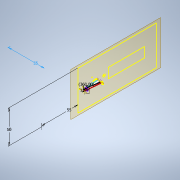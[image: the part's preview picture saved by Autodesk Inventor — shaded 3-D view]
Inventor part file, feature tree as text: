
AUTODESK INVENTOR PART (.ipt)
format: ipt  version: 2021 (Build 250183000, 183)  size: 411,136 bytes
history: native  units: mm
features: other x14, sketch x12, sweep x4, reference x2
ambient origin geometry x8: Origin, YZ Plane, XZ Plane, XY Plane, X Axis, Y Axis, Z Axis, Center Point
bodies: Body1 (feature_tree)
feature tree (32):
  sketch  "Szkic1"
  other  "Płaszczyzna konstrukcyjna1"
  sketch  "Szkic2"
  other  "Płaszczyzna konstrukcyjna2"
  sketch  "Szkic3"
  sketch  "Szkic 3D1"
  other  "Płaszczyzna konstrukcyjna3"
  sketch  "Szkic4"
  other  "Płaszczyzna konstrukcyjna4"
  sketch  "Szkic5"
  other  "Płaszczyzna konstrukcyjna5"
  sweep  "Przeciągnięcie2"
  sweep  "Przeciągnięcie3"
  sweep  "Przeciągnięcie4"
  other  "Płaszczyzna konstrukcyjna6"
  sweep  "Przeciągnięcie5"
  sketch  "Szkic 3D3"
  other  "Płaszczyzna konstrukcyjna7"
  sketch  "Szkic8"
  other  "Płaszczyzna konstrukcyjna8"
  sketch  "Szkic9"
  other  "Oś konstrukcyjna1"
  reference  "Odniesienie1"
  sketch  "Szkic6"
  sketch  "Szkic7"
  sketch  "Szkic 3D2"
  reference  "Odniesienie2"
  parser-record x1  (decoder bookkeeping rows leaked as tree rows — omitted from the tree; the rows remain in map.json)
  other  "model tensometru.iam"
  other  "zalany_tensometr:1"
  other  "podstwa:1"
  other  "tensometr:1"
note: 1 file-system path scrubbed to <path> (originals preserved in map.json)
